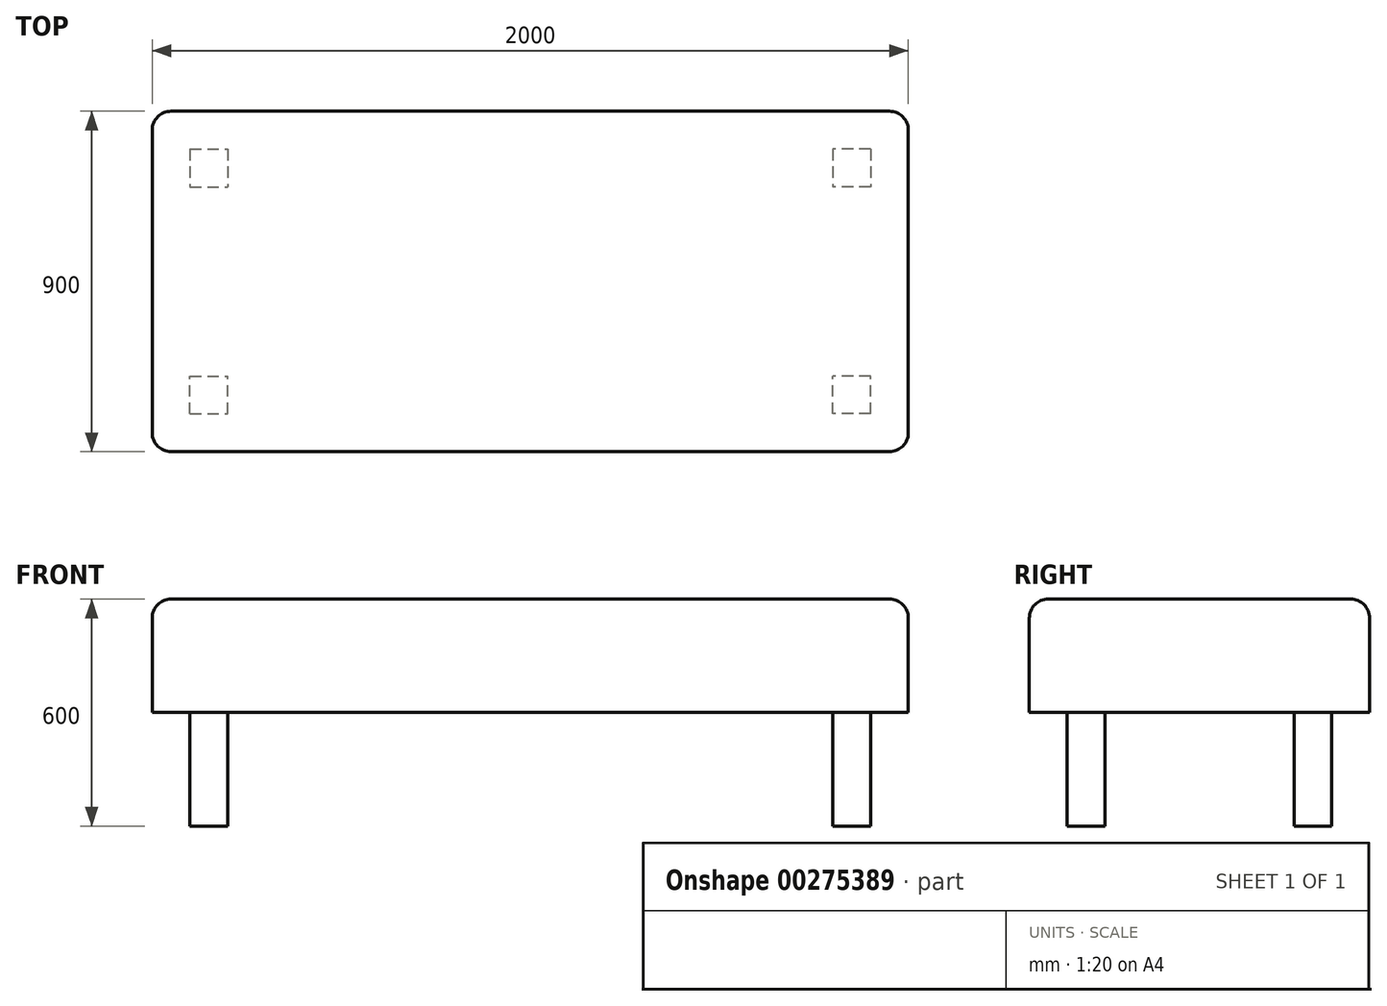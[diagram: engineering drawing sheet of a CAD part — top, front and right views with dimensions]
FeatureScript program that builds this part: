
annotation { "Feature Type Name" : "Feature", "Feature Type Description" : "" }
export const myFeature = defineFeature(function(context is Context, id is Id, definition is map)
    precondition{}
    {
        {
            var Q0;
            Q0=qCreatedBy(makeId("Top.planeOp"),FACE);
            var sketch = newSketch(context, id + "F0", { "sketchPlane" : qUnion([Q0])});
            skLineSegment(sketch, "E0.bottom", {"start": v(1000, 450) * mm, "end": v(-1000, 450) * mm});
            skLineSegment(sketch, "E0.top", {"start": v(1000, -450) * mm, "end": v(-1000, -450) * mm});
            skLineSegment(sketch, "E0.left", {"start": v(1000, 450) * mm, "end": v(1000, -450) * mm});
            skLineSegment(sketch, "E0.right", {"start": v(-1000, 450) * mm, "end": v(-1000, -450) * mm});
            skPoint(sketch, "E0.middle", {"position": v(0, 0) * mm});
            skSolve(sketch);
        }
        {
            var Q0;
            Q0=qSketchRegion(id+"F0",true);
            extrude(context, id + "F1", {"entities" : qUnion([Q0]), "depth" : 300 * mm});
        }
        {
            var Q0;
            Q0=makeQuery(id+"F1.opExtrude","CAP_FACE",FACE,{"disambiguationData":[OSD([sQuery(id+"F0.wireOp",EDGE,"E0.bottom"),sQuery(id+"F0.wireOp",EDGE,"E0.top"),sQuery(id+"F0.wireOp",EDGE,"E0.left"),sQuery(id+"F0.wireOp",EDGE,"E0.right")])],"isStart":false});
            var Q1;
            Q1=makeQuery(id+"F1.opExtrude","SWEPT_EDGE",EDGE,{"disambiguationData":[OSD([sQuery(id+"F0.wireOp",EDGE,"E0.top"),sQuery(id+"F0.wireOp",EDGE,"E0.right")])]});
            var Q2;
            Q2=makeQuery(id+"F1.opExtrude","SWEPT_EDGE",EDGE,{"disambiguationData":[OSD([sQuery(id+"F0.wireOp",EDGE,"E0.top"),sQuery(id+"F0.wireOp",EDGE,"E0.left")])]});
            var Q3;
            Q3=makeQuery(id+"F1.opExtrude","SWEPT_EDGE",EDGE,{"disambiguationData":[OSD([sQuery(id+"F0.wireOp",EDGE,"E0.bottom"),sQuery(id+"F0.wireOp",EDGE,"E0.left")])]});
            var Q4;
            Q4=makeQuery(id+"F1.opExtrude","SWEPT_EDGE",EDGE,{"disambiguationData":[OSD([sQuery(id+"F0.wireOp",EDGE,"E0.bottom"),sQuery(id+"F0.wireOp",EDGE,"E0.right")])]});
            fillet(context, id + "F2", {"entities" : qUnion([Q0, Q1, Q2, Q3, Q4]), "radius" : 50 * mm, "tangentPropagation" : true, "allowEdgeOverflow" : false});
        }
        {
            var Q0;
            Q0=makeQuery(id+"F1.opExtrude","CAP_FACE",FACE,{"disambiguationData":[OSD([sQuery(id+"F0.wireOp",EDGE,"E0.bottom"),sQuery(id+"F0.wireOp",EDGE,"E0.top"),sQuery(id+"F0.wireOp",EDGE,"E0.left"),sQuery(id+"F0.wireOp",EDGE,"E0.right")])],"isStart":true});
            var sketch = newSketch(context, id + "F3", { "sketchPlane" : qUnion([Q0])});
            skLineSegment(sketch, "E1.bottom", {"start": v(-900, 350) * mm, "end": v(-800, 350) * mm});
            skLineSegment(sketch, "E1.top", {"start": v(-900, 250) * mm, "end": v(-800, 250) * mm});
            skLineSegment(sketch, "E1.left", {"start": v(-900, 350) * mm, "end": v(-900, 250) * mm});
            skLineSegment(sketch, "E1.right", {"start": v(-800, 350) * mm, "end": v(-800, 250) * mm});
            skLineSegment(sketch, "E2", {"start": v(-1552.23, 0) * mm, "end": v(1382.63, 0) * mm, "construction": true});
            skLineSegment(sketch, "E3", {"start": v(0, 891.9) * mm, "end": v(0, -789.68) * mm, "construction": true});
            skLineSegment(sketch, "E4.MirrorCS", {"start": v(900, 350) * mm, "end": v(800, 350) * mm});
            skLineSegment(sketch, "E5.MirrorCS", {"start": v(800, 350) * mm, "end": v(800, 250) * mm});
            skLineSegment(sketch, "E6.MirrorCS", {"start": v(900, 250) * mm, "end": v(800, 250) * mm});
            skLineSegment(sketch, "E7.MirrorCS", {"start": v(900, 350) * mm, "end": v(900, 250) * mm});
            skLineSegment(sketch, "E8.MirrorCS", {"start": v(-900, -350) * mm, "end": v(-800, -350) * mm});
            skLineSegment(sketch, "E9.MirrorCS", {"start": v(-900, -250) * mm, "end": v(-800, -250) * mm});
            skLineSegment(sketch, "E10.MirrorCS", {"start": v(-900, -350) * mm, "end": v(-900, -250) * mm});
            skLineSegment(sketch, "E11.MirrorCS", {"start": v(-800, -350) * mm, "end": v(-800, -250) * mm});
            skLineSegment(sketch, "E12.MirrorCS", {"start": v(900, -350) * mm, "end": v(900, -250) * mm});
            skLineSegment(sketch, "E13.MirrorCS", {"start": v(900, -250) * mm, "end": v(800, -250) * mm});
            skLineSegment(sketch, "E14.MirrorCS", {"start": v(800, -350) * mm, "end": v(800, -250) * mm});
            skLineSegment(sketch, "E15.MirrorCS", {"start": v(900, -350) * mm, "end": v(800, -350) * mm});
            skSolve(sketch);
        }
        {
            var Q0;
            Q0=qSketchRegion(id+"F3",true);
            extrude(context, id + "F4", {"entities" : qUnion([Q0]), "operationType" : NewBodyOperationType.ADD, "depth" : 300 * mm});
        }
    });
